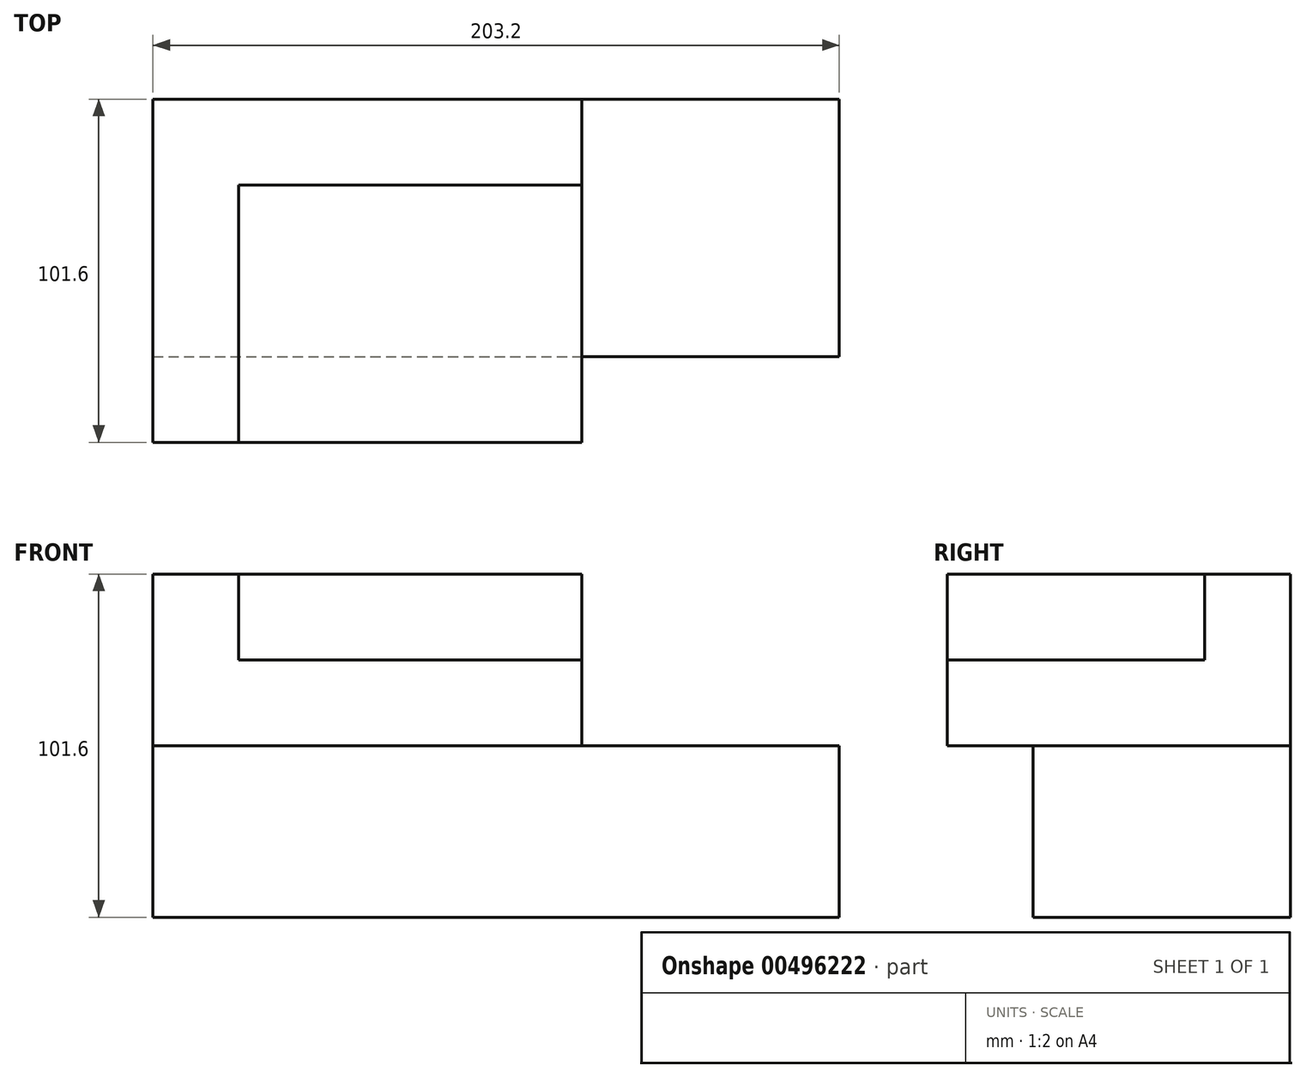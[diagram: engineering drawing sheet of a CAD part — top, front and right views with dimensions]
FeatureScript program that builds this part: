
annotation { "Feature Type Name" : "Feature", "Feature Type Description" : "" }
export const myFeature = defineFeature(function(context is Context, id is Id, definition is map)
    precondition{}
    {
        {
            var Q0;
            Q0=qCreatedBy(makeId("Top.planeOp"),FACE);
            var sketch = newSketch(context, id + "F0", { "sketchPlane" : qUnion([Q0])});
            skLineSegment(sketch, "E0.bottom", {"start": v(-131.14, 52.14) * mm, "end": v(72.06, 52.14) * mm});
            skLineSegment(sketch, "E0.top", {"start": v(-131.14, -24.06) * mm, "end": v(72.06, -24.06) * mm});
            skLineSegment(sketch, "E0.left", {"start": v(-131.14, 52.14) * mm, "end": v(-131.14, -24.06) * mm});
            skLineSegment(sketch, "E0.right", {"start": v(72.06, 52.14) * mm, "end": v(72.06, -24.06) * mm});
            skSolve(sketch);
        }
        {
            var Q0;
            Q0 = qSketchRegion(id + "F0", true);
            extrude(context, id + "F1", {"entities" : qUnion([Q0]), "depth" : 50.8 * mm});
        }
        {
            var Q0;
            Q0=makeQuery(id+"F1.opExtrude","CAP_FACE",FACE,{"disambiguationData":[OSD([sQuery(id+"F0.wireOp",EDGE,"E0.bottom"),sQuery(id+"F0.wireOp",EDGE,"E0.top"),sQuery(id+"F0.wireOp",EDGE,"E0.left"),sQuery(id+"F0.wireOp",EDGE,"E0.right")])],"isStart":false});
            var sketch = newSketch(context, id + "F2", { "sketchPlane" : qUnion([Q0])});
            skLineSegment(sketch, "E1.bottom", {"start": v(-131.14, 52.14) * mm, "end": v(-4.14, 52.14) * mm});
            skLineSegment(sketch, "E1.top", {"start": v(-131.14, -49.46) * mm, "end": v(-4.14, -49.46) * mm});
            skLineSegment(sketch, "E1.left", {"start": v(-131.14, 52.14) * mm, "end": v(-131.14, -49.46) * mm});
            skLineSegment(sketch, "E1.right", {"start": v(-4.14, 52.14) * mm, "end": v(-4.14, -49.46) * mm});
            skSolve(sketch);
        }
        {
            var Q0;
            Q0 = qSketchRegion(id + "F2", true);
            extrude(context, id + "F3", {"entities" : qUnion([Q0]), "operationType" : NewBodyOperationType.ADD, "depth" : 50.8 * mm});
        }
        {
            var Q0;
            Q0=makeQuery(id+"F3.opExtrude","SWEPT_FACE",FACE,{"disambiguationData":[OSD([sQuery(id+"F2.wireOp",EDGE,"E1.right")])]});
            var sketch = newSketch(context, id + "F4", { "sketchPlane" : qUnion([Q0])});
            skLineSegment(sketch, "E2.bottom", {"start": v(-49.46, 76.2) * mm, "end": v(26.74, 76.2) * mm});
            skLineSegment(sketch, "E2.top", {"start": v(-49.46, 101.6) * mm, "end": v(26.74, 101.6) * mm});
            skLineSegment(sketch, "E2.left", {"start": v(-49.46, 76.2) * mm, "end": v(-49.46, 101.6) * mm});
            skLineSegment(sketch, "E2.right", {"start": v(26.74, 76.2) * mm, "end": v(26.74, 101.6) * mm});
            skSolve(sketch);
        }
        {
            var Q0;
            Q0 = qSketchRegion(id + "F4", true);
            extrude(context, id + "F5", {"entities" : qUnion([Q0]), "operationType" : NewBodyOperationType.REMOVE, "oppositeDirection" : true, "depth" : 101.6 * mm});
        }
    });
